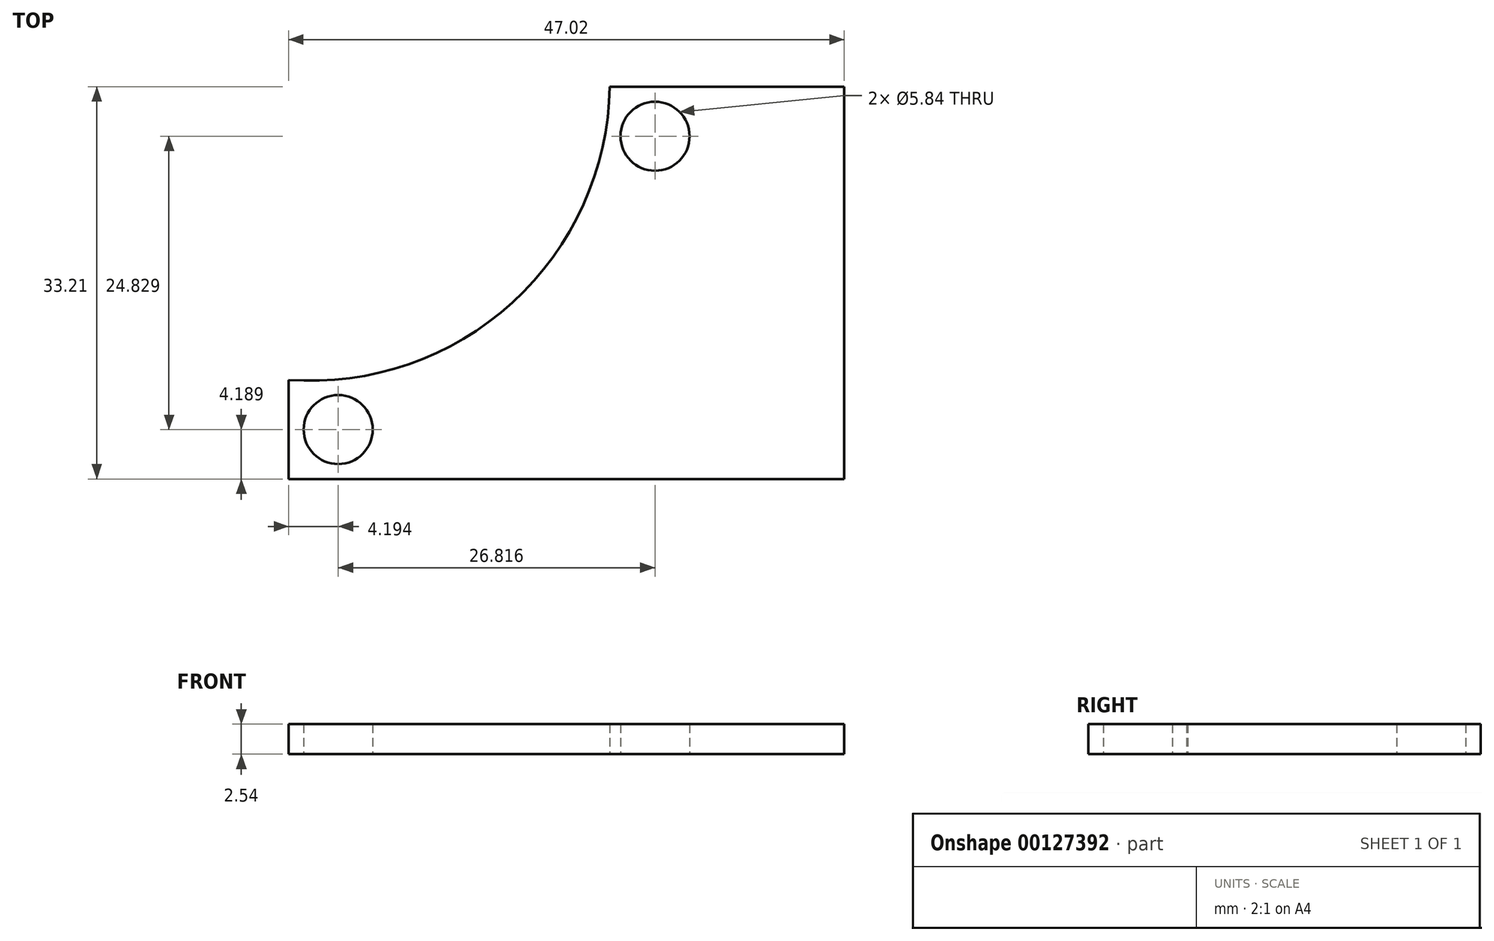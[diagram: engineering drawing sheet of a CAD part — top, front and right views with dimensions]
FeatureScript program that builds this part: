
annotation { "Feature Type Name" : "Feature", "Feature Type Description" : "" }
export const myFeature = defineFeature(function(context is Context, id is Id, definition is map)
    precondition{}
    {
        {
            var Q0;
            Q0=qCreatedBy(makeId("Top.planeOp"),FACE);
            var sketch = newSketch(context, id + "F0", { "sketchPlane" : qUnion([Q0])});
            skLineSegment(sketch, "E0.bottom", {"start": v(16, 19.73) * mm, "end": v(-31, 19.73) * mm});
            skLineSegment(sketch, "E0.top", {"start": v(16, -13.48) * mm, "end": v(-31, -13.48) * mm});
            skLineSegment(sketch, "E0.left", {"start": v(16, 19.73) * mm, "end": v(16, -13.48) * mm});
            skLineSegment(sketch, "E0.right", {"start": v(-31, 19.73) * mm, "end": v(-31, -13.48) * mm});
            skArc(sketch, "E1", {"start": v(-31, -5.09) * mm, "mid": v(-12.07, 1.46) * mm, "end": v(-3.83, 19.73) * mm});
            skCircle(sketch, "E2", {"center": v(0, 15.54) * mm, "radius": 2.92 * mm});
            skCircle(sketch, "E3", {"center": v(-26.82, -9.3) * mm, "radius": 2.92 * mm});
            skSolve(sketch);
        }
        {
            var Q0;
            {var subQ1=sQuery(id+"F0.wireOp",EDGE,"E0.top");Q0=makeQuery(id+"F0.imprint","IMPRINT",FACE,{"disambiguationData":[TD([[makeQuery(id+"F0.imprint","IMPRINT",EDGE,{"derivedFrom":subQ1}),-1.0]])]});}
            extrude(context, id + "F1", {"entities" : qUnion([Q0]), "endBound" : BoundingType.SYMMETRIC, "depth" : 2.54 * mm});
        }
    });
